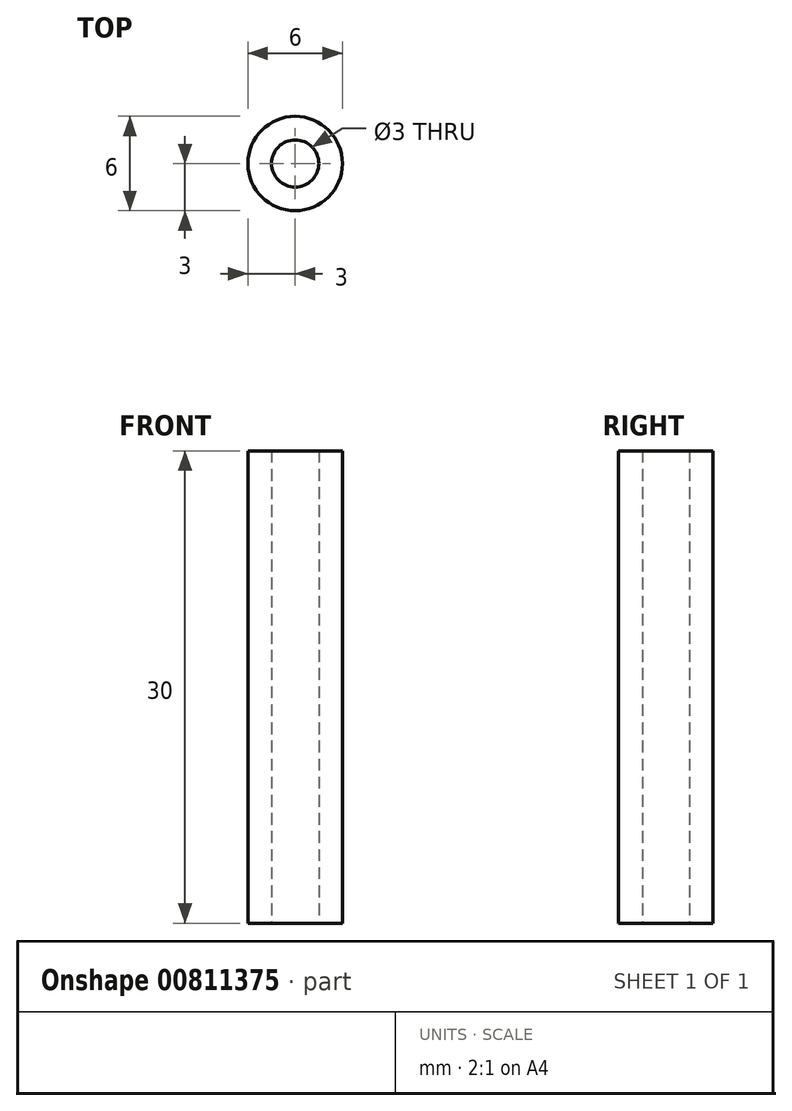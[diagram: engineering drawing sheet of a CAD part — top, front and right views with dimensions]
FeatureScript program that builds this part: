
annotation { "Feature Type Name" : "Feature", "Feature Type Description" : "" }
export const myFeature = defineFeature(function(context is Context, id is Id, definition is map)
    precondition{}
    {
        {
            var Q0;
            Q0=qCreatedBy(makeId("Top.planeOp"),FACE);
            var sketch = newSketch(context, id + "F0", { "sketchPlane" : qUnion([Q0])});
            skCircle(sketch, "E0", {"center": v(0, 0) * mm, "radius": 1.5 * mm});
            skCircle(sketch, "E1", {"center": v(0, 0) * mm, "radius": 3 * mm});
            skSolve(sketch);
        }
        {
            var Q0;
            Q0=makeQuery(id+"F0.imprint","IMPRINT",FACE,{"disambiguationData":[TD([[makeQuery(id+"F0.imprint","IMPRINT",EDGE,{"derivedFrom":sQuery(id+"F0.wireOp",EDGE,"E0")}),-1.0]])]});
            extrude(context, id + "F1", {"entities" : qUnion([Q0]), "depth" : 30 * mm, "offsetDistance" : 25 * mm});
        }
    });
